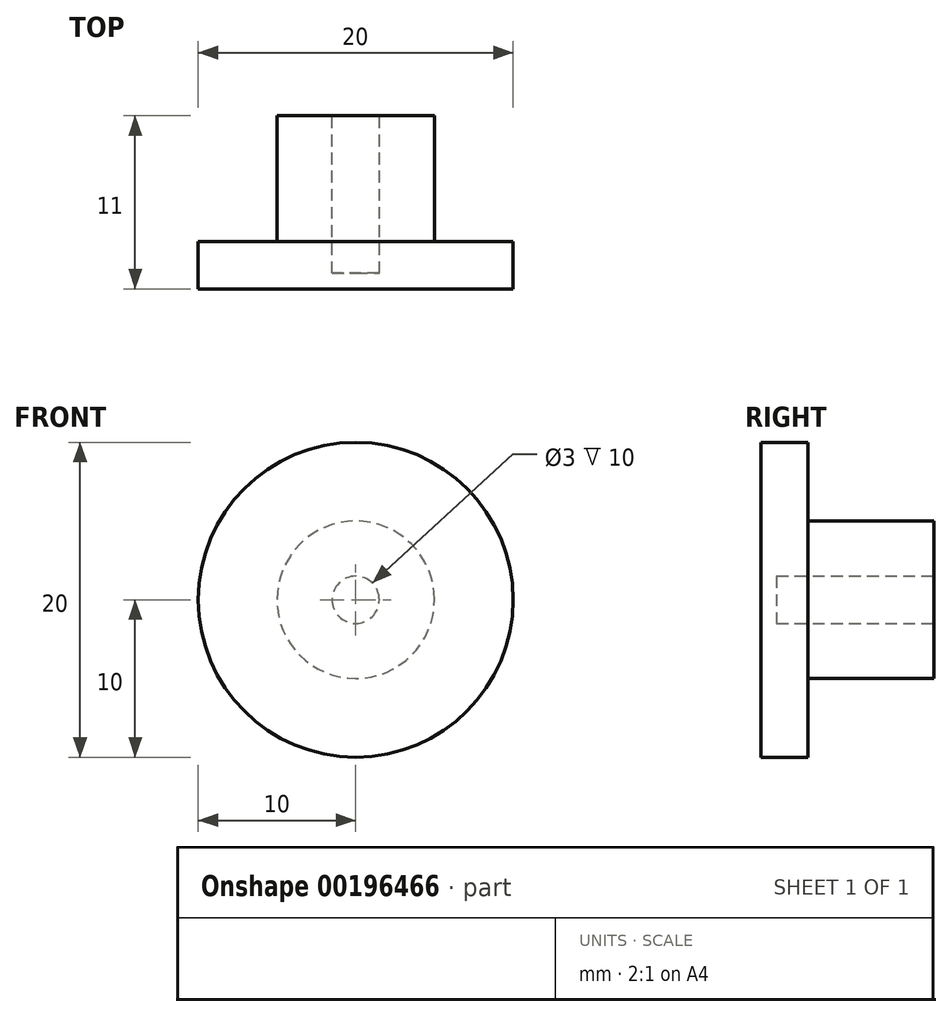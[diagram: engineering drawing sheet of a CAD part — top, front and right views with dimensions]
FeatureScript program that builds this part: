
annotation { "Feature Type Name" : "Feature", "Feature Type Description" : "" }
export const myFeature = defineFeature(function(context is Context, id is Id, definition is map)
    precondition{}
    {
        {
            var Q0;
            Q0=qCreatedBy(makeId("Front.planeOp"),FACE);
            var sketch = newSketch(context, id + "F0", { "sketchPlane" : qUnion([Q0])});
            skCircle(sketch, "E0", {"center": v(0, 0) * mm, "radius": 5 * mm});
            skSolve(sketch);
        }
        {
            var Q0;
            Q0 = qSketchRegion(id + "F0", true);
            extrude(context, id + "F1", {"entities" : qUnion([Q0]), "depth" : 8 * mm});
        }
        {
            var Q0;
            Q0=makeQuery(id+"F1.opExtrude","CAP_FACE",FACE,{"disambiguationData":[OSD([sQuery(id+"F0.wireOp",EDGE,"E0")])],"isStart":false});
            var sketch = newSketch(context, id + "F2", { "sketchPlane" : qUnion([Q0])});
            skCircle(sketch, "E1", {"center": v(0, 0) * mm, "radius": 10 * mm});
            skSolve(sketch);
        }
        {
            var Q0;
            Q0 = qSketchRegion(id + "F2", true);
            extrude(context, id + "F3", {"entities" : qUnion([Q0]), "operationType" : NewBodyOperationType.ADD, "depth" : 3 * mm});
        }
        {
            var Q0;
            Q0=makeQuery(id+"F1.opExtrude","CAP_FACE",FACE,{"disambiguationData":[OSD([sQuery(id+"F0.wireOp",EDGE,"E0")])],"isStart":true});
            var sketch = newSketch(context, id + "F4", { "sketchPlane" : qUnion([Q0])});
            skCircle(sketch, "E2", {"center": v(0, 0) * mm, "radius": 1.5 * mm});
            skSolve(sketch);
        }
        {
            var Q0;
            Q0 = qSketchRegion(id + "F4", true);
            extrude(context, id + "F5", {"entities" : qUnion([Q0]), "operationType" : NewBodyOperationType.REMOVE, "oppositeDirection" : true, "depth" : 10 * mm});
        }
    });
